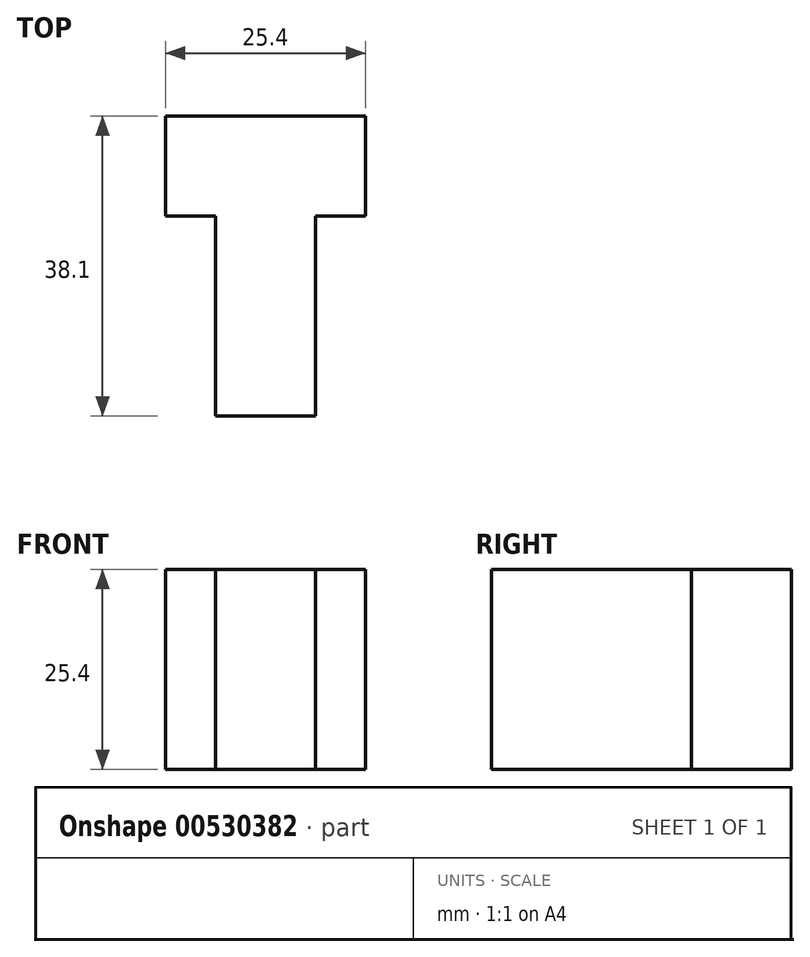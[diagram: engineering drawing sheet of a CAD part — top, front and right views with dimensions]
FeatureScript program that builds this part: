
annotation { "Feature Type Name" : "Feature", "Feature Type Description" : "" }
export const myFeature = defineFeature(function(context is Context, id is Id, definition is map)
    precondition{}
    {
        {
            var Q0;
            Q0=qCreatedBy(makeId("Top.planeOp"),FACE);
            var sketch = newSketch(context, id + "F0", { "sketchPlane" : qUnion([Q0])});
            skLineSegment(sketch, "E0", {"start": v(-12.7, 0) * mm, "end": v(-12.7, -25.4) * mm});
            skLineSegment(sketch, "E1", {"start": v(-12.7, -25.4) * mm, "end": v(0, -25.4) * mm});
            skLineSegment(sketch, "E2", {"start": v(0, -25.4) * mm, "end": v(0, 0) * mm});
            skLineSegment(sketch, "E3", {"start": v(0, 0) * mm, "end": v(6.35, 0) * mm});
            skLineSegment(sketch, "E4", {"start": v(6.35, 0) * mm, "end": v(6.35, 12.7) * mm});
            skLineSegment(sketch, "E5", {"start": v(6.35, 12.7) * mm, "end": v(-19.05, 12.7) * mm});
            skLineSegment(sketch, "E6", {"start": v(-19.05, 12.7) * mm, "end": v(-19.05, 0) * mm});
            skLineSegment(sketch, "E7", {"start": v(-19.05, 0) * mm, "end": v(-12.7, 0) * mm});
            skSolve(sketch);
        }
        {
            var Q0;
            Q0=makeQuery(id+"F0.imprint","IMPRINT",FACE,{"disambiguationData":[TD([[makeQuery(id+"F0.imprint","IMPRINT",EDGE,{"derivedFrom":sQuery(id+"F0.wireOp",EDGE,"E0")}),1.0]])]});
            extrude(context, id + "F1", {"entities" : qUnion([Q0]), "depth" : 25.4 * mm, "offsetDistance" : 25.4 * mm});
        }
    });
